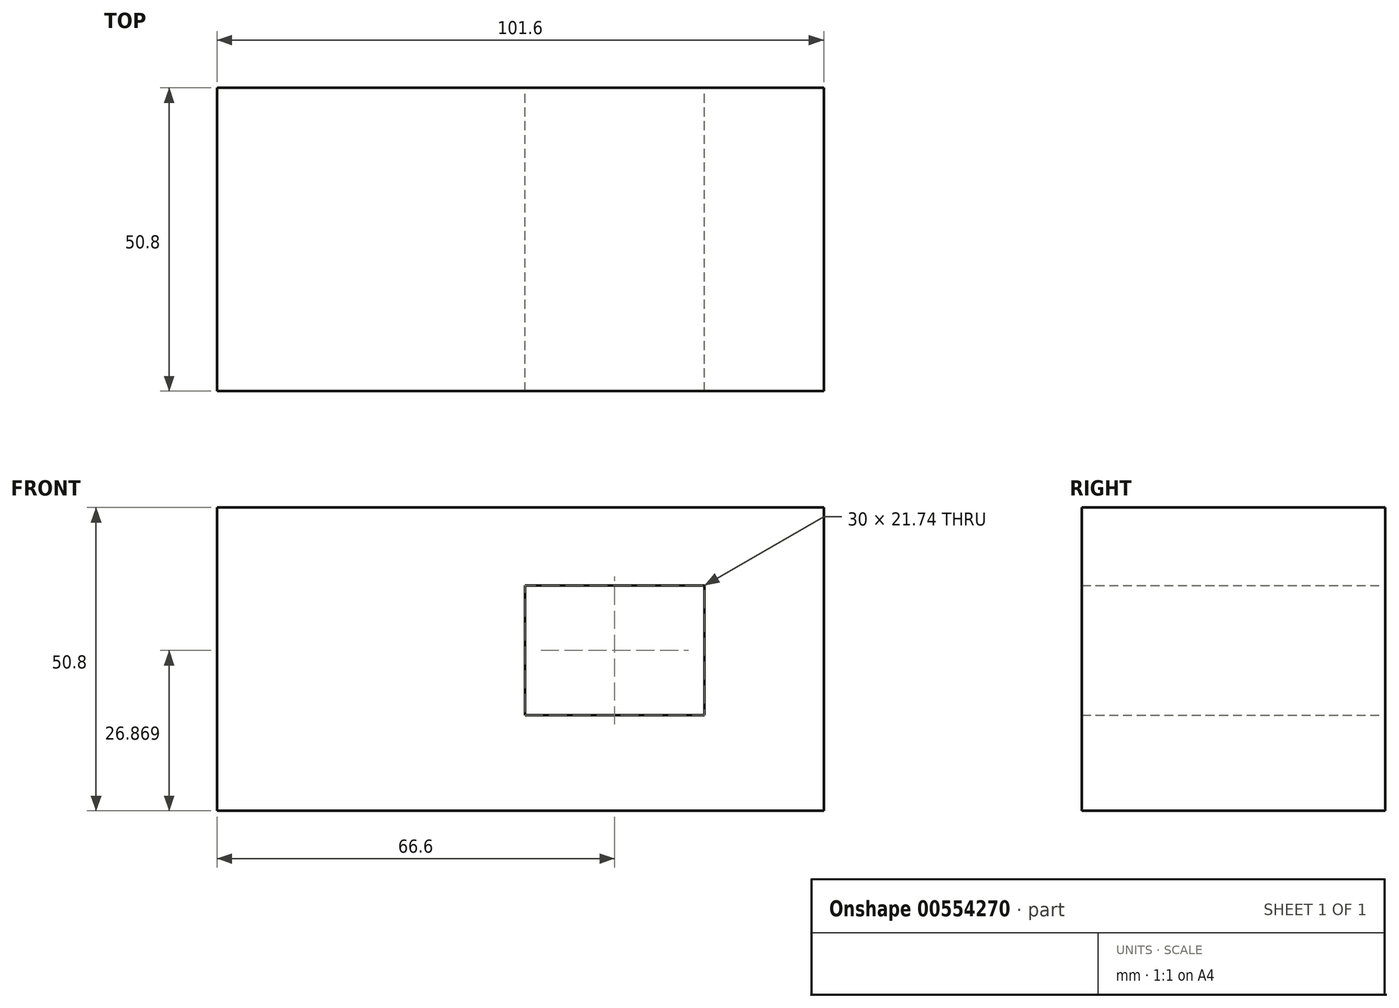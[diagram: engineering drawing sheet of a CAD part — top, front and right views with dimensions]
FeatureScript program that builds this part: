
annotation { "Feature Type Name" : "Feature", "Feature Type Description" : "" }
export const myFeature = defineFeature(function(context is Context, id is Id, definition is map)
    precondition{}
    {
        {
            var Q0;
            Q0=qCreatedBy(makeId("Top.planeOp"),FACE);
            var sketch = newSketch(context, id + "F0", { "sketchPlane" : qUnion([Q0])});
            skSolve(sketch);
        }
        {
            var Q0;
            Q0=qCreatedBy(makeId("Top.planeOp"),FACE);
            var sketch = newSketch(context, id + "F1", { "sketchPlane" : qUnion([Q0])});
            skLineSegment(sketch, "E0.bottom", {"start": v(0, 0) * mm, "end": v(101.6, 0) * mm});
            skLineSegment(sketch, "E0.top", {"start": v(0, 50.8) * mm, "end": v(101.6, 50.8) * mm});
            skLineSegment(sketch, "E0.left", {"start": v(0, 0) * mm, "end": v(0, 50.8) * mm});
            skLineSegment(sketch, "E0.right", {"start": v(101.6, 0) * mm, "end": v(101.6, 50.8) * mm});
            skSolve(sketch);
        }
        {
            var Q0;
            Q0=makeQuery(id+"F1.imprint","IMPRINT",FACE,{"disambiguationData":[TD([[makeQuery(id+"F1.imprint","IMPRINT",EDGE,{"derivedFrom":sQuery(id+"F1.wireOp",EDGE,"E0.bottom")}),1.0]])]});
            extrude(context, id + "F2", {"entities" : qUnion([Q0]), "depth" : 50.8 * mm, "offsetDistance" : 25.4 * mm});
        }
        {
            var Q0;
            Q0=makeQuery(id+"F2.opExtrude","SWEPT_FACE",FACE,{"disambiguationData":[OSD([sQuery(id+"F1.wireOp",EDGE,"E0.top")])]});
            var sketch = newSketch(context, id + "F3", { "sketchPlane" : qUnion([Q0])});
            skLineSegment(sketch, "E1.bottom", {"start": v(-81.6, 16) * mm, "end": v(-51.6, 16) * mm});
            skLineSegment(sketch, "E1.top", {"start": v(-81.6, 37.74) * mm, "end": v(-51.6, 37.74) * mm});
            skLineSegment(sketch, "E1.left", {"start": v(-81.6, 16) * mm, "end": v(-81.6, 37.74) * mm});
            skLineSegment(sketch, "E1.right", {"start": v(-51.6, 16) * mm, "end": v(-51.6, 37.74) * mm});
            skSolve(sketch);
        }
        {
            var Q0;
            Q0 = qSketchRegion(id + "F0", true);
            var Q1;
            Q1=makeQuery(id+"F3.imprint","IMPRINT",FACE,{"disambiguationData":[TD([[makeQuery(id+"F3.imprint","IMPRINT",EDGE,{"derivedFrom":sQuery(id+"F3.wireOp",EDGE,"E1.bottom")}),1.0]])]});
            extrude(context, id + "F4", {"entities" : qUnion([Q0, Q1]), "operationType" : NewBodyOperationType.REMOVE, "endBound" : BoundingType.UP_TO_NEXT, "oppositeDirection" : true, "depth" : 25 * mm, "offsetDistance" : 25 * mm});
        }
    });
